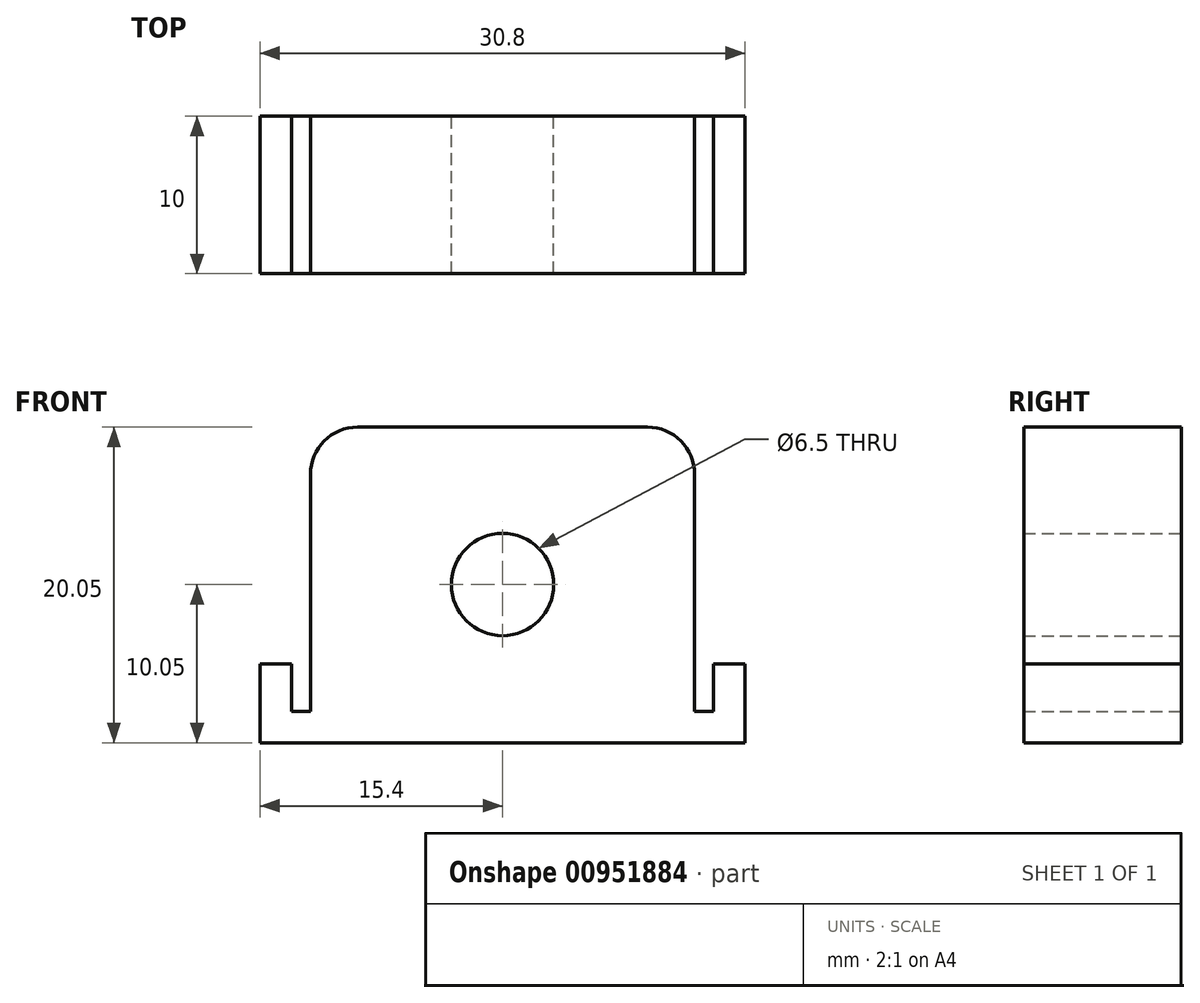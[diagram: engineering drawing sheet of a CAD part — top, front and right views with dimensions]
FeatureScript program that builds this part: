
annotation { "Feature Type Name" : "Feature", "Feature Type Description" : "" }
export const myFeature = defineFeature(function(context is Context, id is Id, definition is map)
    precondition{}
    {
        {
            var Q0;
            Q0=qCreatedBy(makeId("Front.planeOp"),FACE);
            var sketch = newSketch(context, id + "F0", { "sketchPlane" : qUnion([Q0])});
            skLineSegment(sketch, "E0.0", {"start": v(-13.4, -6.54) * mm, "end": v(-13.4, -9.5) * mm});
            skLineSegment(sketch, "E0.2", {"start": v(13.4, -6.54) * mm, "end": v(13.4, -9.5) * mm});
            skLineSegment(sketch, "E1.0", {"start": v(-12.2, 5.5) * mm, "end": v(-12.2, -9.5) * mm});
            skLineSegment(sketch, "E1.1", {"start": v(-9.2, 8.5) * mm, "end": v(9.2, 8.5) * mm});
            skLineSegment(sketch, "E1.2", {"start": v(12.2, 5.5) * mm, "end": v(12.2, -9.5) * mm});
            skArc(sketch, "E2.filletArc", {"start": v(-9.2, 8.5) * mm, "mid": v(-11.32, 7.62) * mm, "end": v(-12.2, 5.5) * mm});
            skArc(sketch, "E3.filletArc", {"start": v(12.2, 5.5) * mm, "mid": v(11.32, 7.62) * mm, "end": v(9.2, 8.5) * mm});
            skLineSegment(sketch, "E4", {"start": v(-13.4, -9.5) * mm, "end": v(-13.4, -9.55) * mm});
            skLineSegment(sketch, "E5", {"start": v(-13.4, -9.55) * mm, "end": v(-12.2, -9.55) * mm});
            skLineSegment(sketch, "E6", {"start": v(-12.2, -9.55) * mm, "end": v(-12.2, -9.5) * mm});
            skLineSegment(sketch, "E7", {"start": v(12.2, -9.5) * mm, "end": v(12.2, -9.55) * mm});
            skLineSegment(sketch, "E8", {"start": v(12.2, -9.55) * mm, "end": v(13.4, -9.55) * mm});
            skLineSegment(sketch, "E9", {"start": v(13.4, -9.55) * mm, "end": v(13.4, -9.5) * mm});
            skLineSegment(sketch, "E10", {"start": v(-13.4, -6.54) * mm, "end": v(-15.4, -6.54) * mm});
            skLineSegment(sketch, "E11", {"start": v(-15.4, -6.54) * mm, "end": v(-15.4, -11.55) * mm});
            skLineSegment(sketch, "E12", {"start": v(13.4, -6.54) * mm, "end": v(15.4, -6.54) * mm});
            skLineSegment(sketch, "E13", {"start": v(15.4, -6.54) * mm, "end": v(15.4, -11.55) * mm});
            skLineSegment(sketch, "E14", {"start": v(-15.4, -11.55) * mm, "end": v(15.4, -11.55) * mm});
            skCircle(sketch, "E15", {"center": v(0, -1.5) * mm, "radius": 3.25 * mm});
            skSolve(sketch);
        }
        {
            var Q0;
            Q0=makeQuery(id+"F0.imprint","IMPRINT",FACE,{"disambiguationData":[TD([[makeQuery(id+"F0.imprint","IMPRINT",EDGE,{"derivedFrom":sQuery(id+"F0.wireOp",EDGE,"E0.0")}),-1.0]])]});
            extrude(context, id + "F1", {"entities" : qUnion([Q0]), "depth" : 10 * mm, "offsetDistance" : 25 * mm});
        }
    });
